# Revit family: FU_Chair_Sandler_Odda 5-1
name_source: partatom
category: Furniture
units: mm (PartAtom-declared; Revit-internal decimal feet)

## family parameters
Always vertical = Yes
Cut with Voids When Loaded = No
OmniClass Number = 23.40.20.00
OmniClass Title = General Furniture and Specialties
Render Appearance Source = Family Geometry
Room Calculation Point = No
Shared = No
Work Plane-Based = No

## types (1)
- Odda 5.1
    Default Elevation = 0 mm  [stored 0 ft]
    Depth = 830 mm  [stored 2.7231 ft]
    Description = Upholstered lounge chair with triangular side panels. Lacquered steel frame.
    Height = 680 mm  [stored 2.23097 ft]
    Manufacturer = Sandler
    Model = Odda 5.1
    URL = https://www.sandlerseating.com
    Width = 960 mm  [stored 3.14961 ft]

note: [stored X ft] marks values corroborated as IEEE doubles in the binary element streams (Revit-internal decimal feet)

## geometry (parser evidence)
native form markers: Sweep x6
no freeform markers — native parametric forms only
